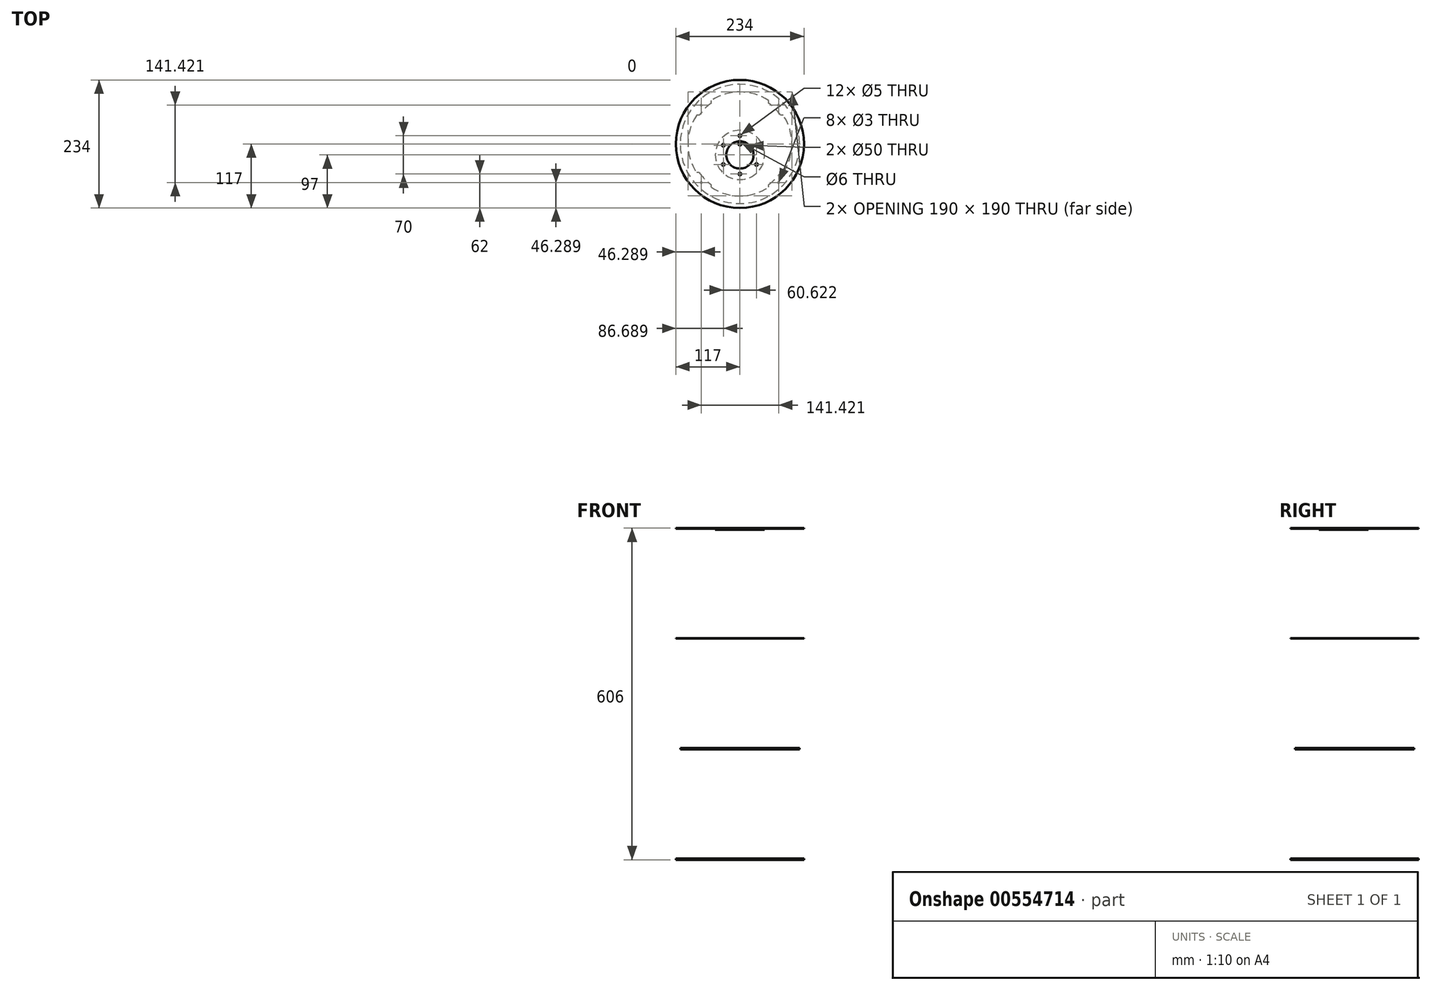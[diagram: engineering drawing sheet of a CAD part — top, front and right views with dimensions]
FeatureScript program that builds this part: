
annotation { "Feature Type Name" : "Feature", "Feature Type Description" : "" }
export const myFeature = defineFeature(function(context is Context, id is Id, definition is map)
    precondition{}
    {
        {
            var Q0;
            Q0=qCreatedBy(makeId("Top.planeOp"),FACE);
            var sketch = newSketch(context, id + "F0", { "sketchPlane" : qUnion([Q0])});
            skCircle(sketch, "E0", {"center": v(0, 0) * mm, "radius": 117 * mm});
            skLineSegment(sketch, "E1", {"start": v(0, -117) * mm, "end": v(0, 117) * mm});
            skCircle(sketch, "E2", {"center": v(0, -20) * mm, "radius": 25 * mm});
            skPoint(sketch, "E3", {"position": v(0, -55) * mm});
            skCircle(sketch, "E4", {"center": v(0, -55) * mm, "radius": 2.5 * mm});
            skCircle(sketch, "E5.1.0", {"center": v(-30.31, -37.5) * mm, "radius": 2.5 * mm});
            skCircle(sketch, "E5.2.0", {"center": v(-30.31, -2.5) * mm, "radius": 2.5 * mm});
            skCircle(sketch, "E5.3.0", {"center": v(0, 15) * mm, "radius": 2.5 * mm});
            skCircle(sketch, "E5.4.0", {"center": v(30.31, -2.5) * mm, "radius": 2.5 * mm});
            skCircle(sketch, "E5.5.0", {"center": v(30.31, -37.5) * mm, "radius": 2.5 * mm});
            skLineSegment(sketch, "E5.anchor1", {"start": v(0, -20) * mm, "end": v(0, -55) * mm, "construction": true});
            skLineSegment(sketch, "E5.anchor2", {"start": v(0, -20) * mm, "end": v(30.31, -37.5) * mm, "construction": true});
            skSolve(sketch);
        }
        {
            var Q0;
            Q0 = qSketchRegion(id + "F0", true);
            var Q1;
            Q1=makeQuery(id+"F0.imprint","IMPRINT",FACE,{"disambiguationData":[TD([[makeQuery(id+"F0.imprint","IMPRINT",EDGE,{"derivedFrom":sQuery(id+"F0.wireOp",EDGE,"E5.4.0")}),-1.0]])]});
            extrude(context, id + "F1", {"entities" : qUnion([Q0, Q1]), "depth" : 1 * mm, "offsetDistance" : 25 * mm});
        }
        {
            var Q0;
            Q0=makeQuery(id+"F1.opExtrude","CAP_FACE",FACE,{"disambiguationData":[OSD([sQuery(id+"F0.wireOp",EDGE,"E0"),sQuery(id+"F0.wireOp",EDGE,"E2"),sQuery(id+"F0.wireOp",EDGE,"E4"),sQuery(id+"F0.wireOp",EDGE,"E5.1.0"),sQuery(id+"F0.wireOp",EDGE,"E5.2.0"),sQuery(id+"F0.wireOp",EDGE,"E5.3.0"),sQuery(id+"F0.wireOp",EDGE,"E5.4.0"),sQuery(id+"F0.wireOp",EDGE,"E5.5.0")])],"isStart":true});
            var sketch = newSketch(context, id + "F2", { "sketchPlane" : qUnion([Q0])});
            skCircle(sketch, "E6.0", {"center": v(0, 20) * mm, "radius": 25 * mm});
            skCircle(sketch, "E7.0", {"center": v(0, 55) * mm, "radius": 2.5 * mm});
            skCircle(sketch, "E8.0", {"center": v(-30.31, 37.5) * mm, "radius": 2.5 * mm});
            skCircle(sketch, "E9.0", {"center": v(-30.31, 2.5) * mm, "radius": 2.5 * mm});
            skCircle(sketch, "E10.0", {"center": v(0, -15) * mm, "radius": 2.5 * mm});
            skCircle(sketch, "E11.0", {"center": v(30.31, 2.5) * mm, "radius": 2.5 * mm});
            skCircle(sketch, "E12.0", {"center": v(30.31, 37.5) * mm, "radius": 2.5 * mm});
            skCircle(sketch, "E13", {"center": v(0, 20) * mm, "radius": 45 * mm});
            skSolve(sketch);
        }
        {
            var Q0;
            Q0 = qSketchRegion(id + "F2", true);
            var Q1;
            Q1=makeQuery(id+"F2.imprint","IMPRINT",FACE,{"disambiguationData":[TD([[makeQuery(id+"F2.imprint","IMPRINT",EDGE,{"derivedFrom":sQuery(id+"F2.wireOp",EDGE,"E6.0")}),1.0]])]});
            extrude(context, id + "F3", {"entities" : qUnion([Q0, Q1]), "depth" : 2 * mm, "offsetDistance" : 25 * mm});
        }
        {
            var Q0;
            Q0=makeQuery(id+"F1.opExtrude","CAP_FACE",FACE,{"disambiguationData":[OSD([sQuery(id+"F0.wireOp",EDGE,"E0"),sQuery(id+"F0.wireOp",EDGE,"E2"),sQuery(id+"F0.wireOp",EDGE,"E4"),sQuery(id+"F0.wireOp",EDGE,"E5.1.0"),sQuery(id+"F0.wireOp",EDGE,"E5.2.0"),sQuery(id+"F0.wireOp",EDGE,"E5.3.0"),sQuery(id+"F0.wireOp",EDGE,"E5.4.0"),sQuery(id+"F0.wireOp",EDGE,"E5.5.0")])],"isStart":true});
            cPlane(context, id + "F4", {"entities" : qUnion([Q0]), "cplaneType" : CPlaneType.OFFSET, "offset" : 200 * mm, "width" : 150 * mm, "height" : 150 * mm});
        }
        {
            var Q0;
            Q0=qCreatedBy(id+"F4.planeOp",FACE);
            var sketch = newSketch(context, id + "F5", { "sketchPlane" : qUnion([Q0])});
            skCircle(sketch, "E14.0.0", {"center": v(0, 0) * mm, "radius": 117 * mm});
            skCircle(sketch, "E15", {"center": v(0, 0) * mm, "radius": 3 * mm});
            skSolve(sketch);
        }
        {
            var Q0;
            Q0 = qSketchRegion(id + "F5", true);
            var Q1;
            Q1=makeQuery(id+"F5.imprint","IMPRINT",FACE,{"disambiguationData":[TD([[makeQuery(id+"F5.imprint","IMPRINT",EDGE,{"derivedFrom":sQuery(id+"F5.wireOp",EDGE,"E14.0.0")}),1.0]])]});
            extrude(context, id + "F6", {"entities" : qUnion([Q0, Q1]), "depth" : 1 * mm, "offsetDistance" : 25 * mm});
        }
        {
            var Q0;
            Q0=makeQuery(id+"F6.opExtrude","CAP_FACE",FACE,{"disambiguationData":[OSD([sQuery(id+"F5.wireOp",EDGE,"E14.0.0")])],"isStart":false});
            cPlane(context, id + "F7", {"entities" : qUnion([Q0]), "cplaneType" : CPlaneType.OFFSET, "offset" : 200 * mm, "width" : 150 * mm, "height" : 150 * mm});
        }
        {
            var Q0;
            Q0=qCreatedBy(id+"F7.planeOp",FACE);
            var sketch = newSketch(context, id + "F8", { "sketchPlane" : qUnion([Q0])});
            skCircle(sketch, "E16.0.0", {"center": v(0, 0) * mm, "radius": 117 * mm});
            skArc(sketch, "E17", {"start": v(-74.33, -52.5) * mm, "mid": v(-64.35, -64.35) * mm, "end": v(-52.5, -74.33) * mm});
            skArc(sketch, "E18", {"start": v(79.18, -52.5) * mm, "mid": v(95, 0) * mm, "end": v(79.18, 52.5) * mm});
            skLineSegment(sketch, "E19.bottom", {"start": v(-52.5, 162.5) * mm, "end": v(52.5, 162.5) * mm});
            skLineSegment(sketch, "E19.top", {"start": v(-52.5, -162.5) * mm, "end": v(52.5, -162.5) * mm});
            skLineSegment(sketch, "E19.left", {"start": v(-52.5, 162.5) * mm, "end": v(-52.5, 104.56) * mm});
            skLineSegment(sketch, "E19.right", {"start": v(52.5, 162.5) * mm, "end": v(52.5, 104.56) * mm});
            skLineSegment(sketch, "E20.bottom", {"start": v(198.13, -52.5) * mm, "end": v(104.56, -52.5) * mm});
            skLineSegment(sketch, "E20.top", {"start": v(198.13, 52.5) * mm, "end": v(104.56, 52.5) * mm});
            skLineSegment(sketch, "E20.left", {"start": v(198.13, -52.5) * mm, "end": v(198.13, 52.5) * mm});
            skLineSegment(sketch, "E20.right", {"start": v(-198.13, -52.5) * mm, "end": v(-198.13, 52.5) * mm});
            skArc(sketch, "E21.trimOffspring", {"start": v(-52.5, 74.33) * mm, "mid": v(-64.35, 64.35) * mm, "end": v(-74.33, 52.5) * mm});
            skArc(sketch, "E22.trimOffspring", {"start": v(74.33, 52.5) * mm, "mid": v(64.35, 64.35) * mm, "end": v(52.5, 74.33) * mm});
            skArc(sketch, "E23.trimOffspring", {"start": v(52.5, -74.33) * mm, "mid": v(64.35, -64.35) * mm, "end": v(74.33, -52.5) * mm});
            skLineSegment(sketch, "E24.trimOffspring", {"start": v(-52.5, -52.5) * mm, "end": v(-79.18, -52.5) * mm});
            skLineSegment(sketch, "E25.trimOffspring", {"start": v(-52.5, -52.5) * mm, "end": v(-52.5, -79.18) * mm});
            skLineSegment(sketch, "E26.trimOffspring", {"start": v(52.5, -52.5) * mm, "end": v(52.5, -79.18) * mm});
            skLineSegment(sketch, "E27.trimOffspring", {"start": v(-52.5, 52.5) * mm, "end": v(-79.18, 52.5) * mm});
            skLineSegment(sketch, "E28.trimOffspring", {"start": v(-52.5, 79.18) * mm, "end": v(-52.5, 52.5) * mm});
            skLineSegment(sketch, "E29.trimOffspring", {"start": v(52.5, 79.18) * mm, "end": v(52.5, 52.5) * mm});
            skLineSegment(sketch, "E30.trimOffspring", {"start": v(-104.56, 52.5) * mm, "end": v(-198.13, 52.5) * mm});
            skLineSegment(sketch, "E31.trimOffspring", {"start": v(-104.56, -52.5) * mm, "end": v(-198.13, -52.5) * mm});
            skLineSegment(sketch, "E32.trimOffspring", {"start": v(-52.5, -104.56) * mm, "end": v(-52.5, -162.5) * mm});
            skLineSegment(sketch, "E33.trimOffspring", {"start": v(52.5, -104.56) * mm, "end": v(52.5, -162.5) * mm});
            skLineSegment(sketch, "E34.trimOffspring", {"start": v(79.18, -52.5) * mm, "end": v(52.5, -52.5) * mm});
            skLineSegment(sketch, "E35.trimOffspring", {"start": v(79.18, 52.5) * mm, "end": v(52.5, 52.5) * mm});
            skArc(sketch, "E36.trimOffspring", {"start": v(52.5, 79.18) * mm, "mid": v(0, 95) * mm, "end": v(-52.5, 79.18) * mm});
            skArc(sketch, "E37.trimOffspring", {"start": v(-79.18, 52.5) * mm, "mid": v(-95, 0) * mm, "end": v(-79.18, -52.5) * mm});
            skArc(sketch, "E38.trimOffspring", {"start": v(-52.5, -79.18) * mm, "mid": v(0, -95) * mm, "end": v(52.5, -79.18) * mm});
            skCircle(sketch, "E39", {"center": v(0, 0) * mm, "radius": 109 * mm});
            skLineSegment(sketch, "E40", {"start": v(0, 0) * mm, "end": v(-52.5, 52.5) * mm, "construction": true});
            skLineSegment(sketch, "E41", {"start": v(-64.35, 64.35) * mm, "end": v(-77.07, 77.07) * mm, "construction": true});
            skLineSegment(sketch, "E42", {"start": v(-99.75, 99.75) * mm, "end": v(-82.73, 82.73) * mm, "construction": true});
            skLineSegment(sketch, "E43", {"start": v(52.5, 52.5) * mm, "end": v(-52.5, -52.5) * mm, "construction": true});
            skLineSegment(sketch, "E44", {"start": v(-64.35, -64.35) * mm, "end": v(-97.53, -97.53) * mm, "construction": true});
            skLineSegment(sketch, "E45", {"start": v(-97.53, -97.53) * mm, "end": v(-82.73, -82.73) * mm, "construction": true});
            skLineSegment(sketch, "E46", {"start": v(64.35, 64.35) * mm, "end": v(77.07, 77.07) * mm, "construction": true});
            skLineSegment(sketch, "E47.trimOffspring", {"start": v(-82.73, 82.73) * mm, "end": v(-99.75, 99.75) * mm, "construction": true});
            skLineSegment(sketch, "E48.trimOffspring", {"start": v(-52.5, 52.5) * mm, "end": v(94.67, -94.67) * mm, "construction": true});
            skLineSegment(sketch, "E49.trimOffspring", {"start": v(-77.07, 77.07) * mm, "end": v(-64.35, 64.35) * mm, "construction": true});
            skLineSegment(sketch, "E50.trimOffspring", {"start": v(-77.07, -77.07) * mm, "end": v(52.5, 52.5) * mm, "construction": true});
            skPoint(sketch, "E51", {"position": v(-70.71, 70.71) * mm});
            skPoint(sketch, "E52", {"position": v(-70.71, -70.71) * mm});
            skPoint(sketch, "E53", {"position": v(70.71, -70.71) * mm});
            skPoint(sketch, "E54", {"position": v(70.71, 70.71) * mm});
            skLineSegment(sketch, "E55", {"start": v(77.07, 77.07) * mm, "end": v(104.56, 104.56) * mm, "construction": true});
            skCircle(sketch, "E56", {"center": v(-70.71, 70.71) * mm, "radius": 1.5 * mm});
            skCircle(sketch, "E57", {"center": v(-70.71, -70.71) * mm, "radius": 1.5 * mm});
            skCircle(sketch, "E58", {"center": v(70.71, -70.71) * mm, "radius": 1.5 * mm});
            skCircle(sketch, "E59", {"center": v(70.71, 70.71) * mm, "radius": 1.5 * mm});
            skSolve(sketch);
        }
        {
            var Q0;
            {var subQ6=sQuery(id+"F8.wireOp",EDGE,"E17");Q0=makeQuery(id+"F8.imprint","IMPRINT",FACE,{"disambiguationData":[TD([[makeQuery(id+"F8.imprint","IMPRINT",EDGE,{"derivedFrom":subQ6}),-1.0]])]});}
            extrude(context, id + "F9", {"entities" : qUnion([Q0]), "depth" : 2 * mm, "offsetDistance" : 25 * mm});
        }
        {
            var Q0;
            Q0=makeQuery(id+"F9.opExtrude","CAP_FACE",FACE,{"disambiguationData":[OSD([sQuery(id+"F8.wireOp",EDGE,"E17"),sQuery(id+"F8.wireOp",EDGE,"E18"),sQuery(id+"F8.wireOp",EDGE,"E21.trimOffspring"),sQuery(id+"F8.wireOp",EDGE,"E22.trimOffspring"),sQuery(id+"F8.wireOp",EDGE,"E23.trimOffspring"),sQuery(id+"F8.wireOp",EDGE,"E24.trimOffspring"),sQuery(id+"F8.wireOp",EDGE,"E25.trimOffspring"),sQuery(id+"F8.wireOp",EDGE,"E26.trimOffspring"),sQuery(id+"F8.wireOp",EDGE,"E27.trimOffspring"),sQuery(id+"F8.wireOp",EDGE,"E28.trimOffspring"),sQuery(id+"F8.wireOp",EDGE,"E29.trimOffspring"),sQuery(id+"F8.wireOp",EDGE,"E34.trimOffspring"),sQuery(id+"F8.wireOp",EDGE,"E35.trimOffspring"),sQuery(id+"F8.wireOp",EDGE,"E36.trimOffspring"),sQuery(id+"F8.wireOp",EDGE,"E37.trimOffspring"),sQuery(id+"F8.wireOp",EDGE,"E38.trimOffspring"),sQuery(id+"F8.wireOp",EDGE,"E39"),sQuery(id+"F8.wireOp",EDGE,"E56"),sQuery(id+"F8.wireOp",EDGE,"E57"),sQuery(id+"F8.wireOp",EDGE,"E58"),sQuery(id+"F8.wireOp",EDGE,"E59")])],"isStart":false});
            cPlane(context, id + "F10", {"entities" : qUnion([Q0]), "cplaneType" : CPlaneType.OFFSET, "offset" : 200 * mm, "width" : 150 * mm, "height" : 150 * mm});
        }
        {
            var Q0;
            Q0=qCreatedBy(id+"F10.planeOp",FACE);
            var sketch = newSketch(context, id + "F11", { "sketchPlane" : qUnion([Q0])});
            skCircle(sketch, "E60.0", {"center": v(-70.71, 70.71) * mm, "radius": 1.5 * mm});
            skCircle(sketch, "E61.0", {"center": v(70.71, 70.71) * mm, "radius": 1.5 * mm});
            skCircle(sketch, "E62.0", {"center": v(70.71, -70.71) * mm, "radius": 1.5 * mm});
            skCircle(sketch, "E63.0", {"center": v(-70.71, -70.71) * mm, "radius": 1.5 * mm});
            skArc(sketch, "E64.0", {"start": v(-79.18, 52.5) * mm, "mid": v(-95, 0) * mm, "end": v(-79.18, -52.5) * mm});
            skArc(sketch, "E65.0", {"start": v(-74.33, -52.5) * mm, "mid": v(-64.35, -64.35) * mm, "end": v(-52.5, -74.33) * mm});
            skArc(sketch, "E66.0", {"start": v(-52.5, -79.18) * mm, "mid": v(0, -95) * mm, "end": v(52.5, -79.18) * mm});
            skArc(sketch, "E67.0", {"start": v(52.5, -74.33) * mm, "mid": v(64.35, -64.35) * mm, "end": v(74.33, -52.5) * mm});
            skArc(sketch, "E68.0", {"start": v(79.18, -52.5) * mm, "mid": v(95, 0) * mm, "end": v(79.18, 52.5) * mm});
            skArc(sketch, "E69.0", {"start": v(74.33, 52.5) * mm, "mid": v(64.35, 64.35) * mm, "end": v(52.5, 74.33) * mm});
            skArc(sketch, "E70.0", {"start": v(52.5, 79.18) * mm, "mid": v(0, 95) * mm, "end": v(-52.5, 79.18) * mm});
            skPoint(sketch, "E71.0", {"position": v(-52.5, 76.75) * mm});
            skLineSegment(sketch, "E72.0", {"start": v(-52.5, 79.18) * mm, "end": v(-52.5, 74.33) * mm});
            skLineSegment(sketch, "E73.0", {"start": v(-74.33, 52.5) * mm, "end": v(-79.18, 52.5) * mm});
            skLineSegment(sketch, "E74.0", {"start": v(-74.33, -52.5) * mm, "end": v(-79.18, -52.5) * mm});
            skLineSegment(sketch, "E75.0", {"start": v(-52.5, -74.33) * mm, "end": v(-52.5, -79.18) * mm});
            skLineSegment(sketch, "E76.0", {"start": v(52.5, -74.33) * mm, "end": v(52.5, -79.18) * mm});
            skLineSegment(sketch, "E77.0", {"start": v(79.18, -52.5) * mm, "end": v(74.33, -52.5) * mm});
            skCircle(sketch, "E78.0", {"center": v(0, 0) * mm, "radius": 117 * mm});
            skArc(sketch, "E79.0", {"start": v(-52.5, 74.33) * mm, "mid": v(-64.35, 64.35) * mm, "end": v(-74.33, 52.5) * mm});
            skLineSegment(sketch, "E80.0", {"start": v(52.5, 79.18) * mm, "end": v(52.5, 74.33) * mm});
            skLineSegment(sketch, "E81.0", {"start": v(79.18, 52.5) * mm, "end": v(74.33, 52.5) * mm});
            skSolve(sketch);
        }
        {
            var Q0;
            Q0=makeQuery(id+"F11.imprint","IMPRINT",FACE,{"disambiguationData":[TD([[makeQuery(id+"F11.imprint","IMPRINT",EDGE,{"derivedFrom":sQuery(id+"F11.wireOp",EDGE,"E60.0")}),-1.0]])]});
            extrude(context, id + "F12", {"entities" : qUnion([Q0]), "depth" : 2 * mm, "offsetDistance" : 25 * mm});
        }
    });
